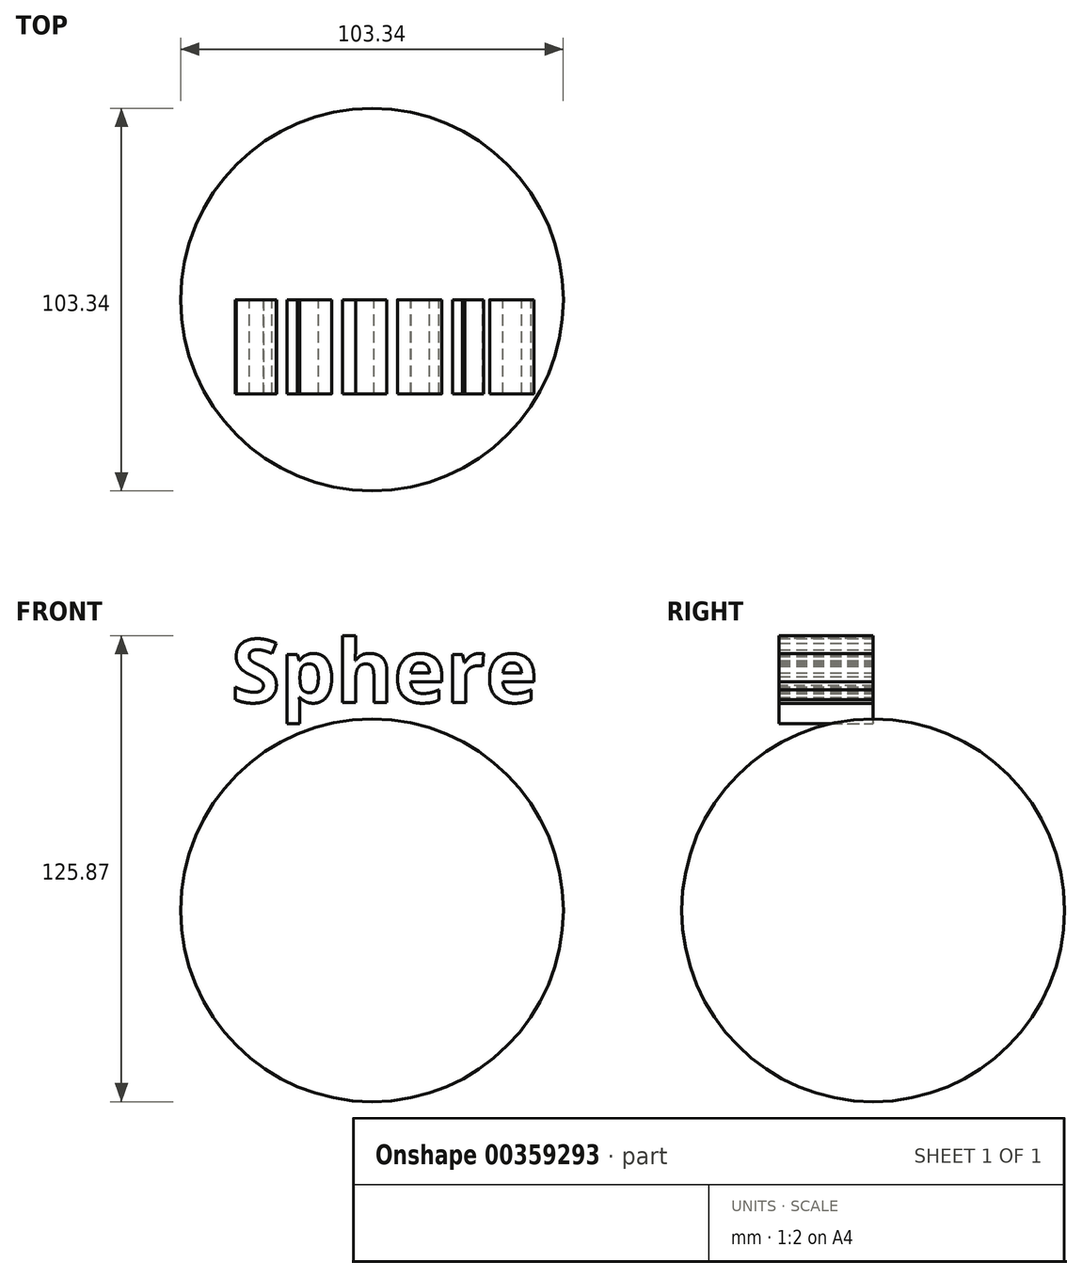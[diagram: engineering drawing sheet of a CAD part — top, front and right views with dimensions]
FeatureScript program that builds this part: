
annotation { "Feature Type Name" : "Feature", "Feature Type Description" : "" }
export const myFeature = defineFeature(function(context is Context, id is Id, definition is map)
    precondition{}
    {
        {
            var Q0;
            Q0=qCreatedBy(makeId("Front.planeOp"),FACE);
            var sketch = newSketch(context, id + "F0", { "sketchPlane" : qUnion([Q0])});
            skCircle(sketch, "E0", {"center": v(0, 0) * mm, "radius": 51.67 * mm});
            skLineSegment(sketch, "E1", {"start": v(0, 51.67) * mm, "end": v(0, -51.67) * mm});
            skSolve(sketch);
        }
        {
            var Q0;
            {var subQ0=sQuery(id+"F0.wireOp",EDGE,"E1");Q0=makeQuery(id+"F0.imprint","IMPRINT",FACE,{"disambiguationData":[TD([[makeQuery(id+"F0.imprint","IMPRINT",EDGE,{"derivedFrom":subQ0}),1.0]])]});}
            var Q1;
            Q1=sQuery(id+"F0.wireOp",EDGE,"E1");
            revolve(context, id + "F1", {"entities" : qUnion([Q0]), "axis" : qUnion([Q1]), "revolveType" : RevolveType.FULL});
        }
        {
            var Q0;
            Q0=qCreatedBy(makeId("Front.planeOp"),FACE);
            var sketch = newSketch(context, id + "F2", { "sketchPlane" : qUnion([Q0])});
            skText(sketch, "E2", { "text": "Sphere", "fontName": "OpenSans-Bold.ttf"});
            const initialGuessF2  = {"E2": [-0.03795, 0.05613, 1, 0, 0.01712]};
            skSetInitialGuess(sketch, initialGuessF2);
            skSolve(sketch);
        }
        {
            var Q0;
            Q0 = qSketchRegion(id + "F2", true);
            extrude(context, id + "F3", {"entities" : qUnion([Q0]), "depth" : 25.4 * mm});
        }
    });
